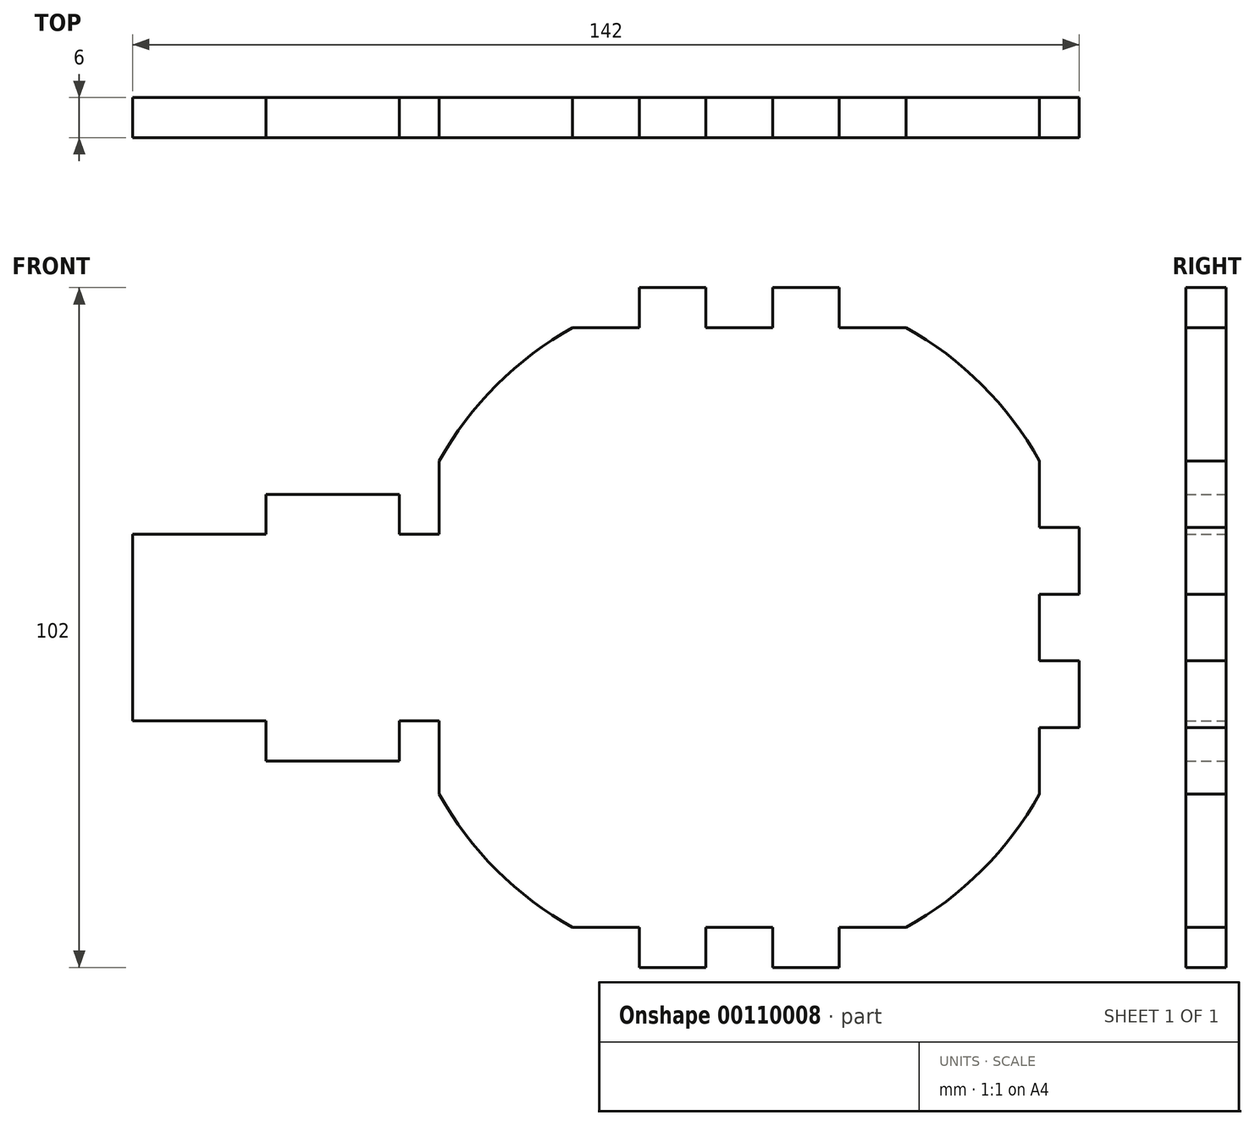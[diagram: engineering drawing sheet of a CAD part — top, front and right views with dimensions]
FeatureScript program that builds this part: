
annotation { "Feature Type Name" : "Feature", "Feature Type Description" : "" }
export const myFeature = defineFeature(function(context is Context, id is Id, definition is map)
    precondition{}
    {
        {
            var Q0;
            Q0=qCreatedBy(makeId("Front.planeOp"),FACE);
            var sketch = newSketch(context, id + "F0", { "sketchPlane" : qUnion([Q0])});
            skLineSegment(sketch, "E0.bottom", {"start": v(53.37, -58.05) * mm, "end": v(43.37, -58.05) * mm});
            skLineSegment(sketch, "E0.top", {"start": v(53.37, 31.95) * mm, "end": v(43.37, 31.95) * mm});
            skLineSegment(sketch, "E0.left", {"start": v(73.37, -38.05) * mm, "end": v(73.37, -28.05) * mm});
            skPoint(sketch, "E0.middle", {"position": v(28.37, -13.05) * mm});
            skArc(sketch, "E1", {"start": v(-16.63, -38.05) * mm, "mid": v(-8.03, -49.46) * mm, "end": v(3.37, -58.05) * mm});
            skPoint(sketch, "E2", {"position": v(-16.63, 11.95) * mm});
            skPoint(sketch, "E3", {"position": v(-16.63, -38.05) * mm});
            skArc(sketch, "E4.trimOffspring", {"start": v(73.37, 11.95) * mm, "mid": v(64.77, 23.35) * mm, "end": v(53.37, 31.95) * mm});
            skArc(sketch, "E5.trimOffspring", {"start": v(3.37, 31.95) * mm, "mid": v(-8.03, 23.35) * mm, "end": v(-16.63, 11.95) * mm});
            skArc(sketch, "E6.trimOffspring", {"start": v(53.37, -58.05) * mm, "mid": v(64.77, -49.46) * mm, "end": v(73.37, -38.05) * mm});
            skPoint(sketch, "E7.orphan", {"position": v(-16.63, -58.05) * mm});
            skPoint(sketch, "E8.orphan", {"position": v(73.37, -58.05) * mm});
            skPoint(sketch, "E9.orphan", {"position": v(73.37, 31.95) * mm});
            skPoint(sketch, "E10.orphan", {"position": v(-16.63, 31.95) * mm});
            skLineSegment(sketch, "E11.top", {"start": v(13.37, 37.95) * mm, "end": v(23.37, 37.95) * mm});
            skLineSegment(sketch, "E11.left", {"start": v(13.37, 37.95) * mm, "end": v(13.37, 31.95) * mm});
            skLineSegment(sketch, "E11.right", {"start": v(23.37, 37.95) * mm, "end": v(23.37, 31.95) * mm});
            skLineSegment(sketch, "E12.trimOffspring", {"start": v(13.37, 31.95) * mm, "end": v(3.37, 31.95) * mm});
            skLineSegment(sketch, "E13.MirrorCS", {"start": v(43.37, 37.95) * mm, "end": v(33.37, 37.95) * mm});
            skLineSegment(sketch, "E14.MirrorCS", {"start": v(43.37, 37.95) * mm, "end": v(43.37, 31.95) * mm});
            skLineSegment(sketch, "E15.MirrorCS", {"start": v(33.37, 37.95) * mm, "end": v(33.37, 31.95) * mm});
            skLineSegment(sketch, "E16.MirrorCS", {"start": v(79.37, 1.95) * mm, "end": v(73.37, 1.95) * mm});
            skLineSegment(sketch, "E17.MirrorCS", {"start": v(79.37, -8.05) * mm, "end": v(73.37, -8.05) * mm});
            skLineSegment(sketch, "E18.MirrorCS", {"start": v(79.37, 1.95) * mm, "end": v(79.37, -8.05) * mm});
            skLineSegment(sketch, "E19.trimOffspring", {"start": v(33.37, 31.95) * mm, "end": v(23.37, 31.95) * mm});
            skLineSegment(sketch, "E20.trimOffspring", {"start": v(73.37, 1.95) * mm, "end": v(73.37, 11.95) * mm});
            skLineSegment(sketch, "E21.MirrorCS", {"start": v(79.37, -18.05) * mm, "end": v(73.37, -18.05) * mm});
            skLineSegment(sketch, "E22.MirrorCS", {"start": v(79.37, -28.05) * mm, "end": v(73.37, -28.05) * mm});
            skLineSegment(sketch, "E23.MirrorCS", {"start": v(79.37, -28.05) * mm, "end": v(79.37, -18.05) * mm});
            skLineSegment(sketch, "E24.MirrorCS", {"start": v(33.37, -64.05) * mm, "end": v(33.37, -58.05) * mm});
            skLineSegment(sketch, "E25.MirrorCS", {"start": v(43.37, -64.05) * mm, "end": v(43.37, -58.05) * mm});
            skLineSegment(sketch, "E26.MirrorCS", {"start": v(13.37, -64.05) * mm, "end": v(13.37, -58.05) * mm});
            skLineSegment(sketch, "E27.MirrorCS", {"start": v(23.37, -64.05) * mm, "end": v(23.37, -58.05) * mm});
            skLineSegment(sketch, "E28.MirrorCS", {"start": v(43.37, -64.05) * mm, "end": v(33.37, -64.05) * mm});
            skLineSegment(sketch, "E29.MirrorCS", {"start": v(13.37, -64.05) * mm, "end": v(23.37, -64.05) * mm});
            skLineSegment(sketch, "E30.trimOffspring", {"start": v(73.37, -18.05) * mm, "end": v(73.37, -8.05) * mm});
            skLineSegment(sketch, "E31.trimOffspring", {"start": v(13.37, -58.05) * mm, "end": v(3.37, -58.05) * mm});
            skLineSegment(sketch, "E32.trimOffspring", {"start": v(33.37, -58.05) * mm, "end": v(23.37, -58.05) * mm});
            skLineSegment(sketch, "E33", {"start": v(-16.63, 11.95) * mm, "end": v(-16.63, 0.95) * mm});
            skLineSegment(sketch, "E34", {"start": v(-16.63, 0.95) * mm, "end": v(-22.63, 0.95) * mm});
            skLineSegment(sketch, "E35", {"start": v(-62.63, 0.95) * mm, "end": v(-62.63, -27.05) * mm});
            skLineSegment(sketch, "E36", {"start": v(-62.63, -27.05) * mm, "end": v(-42.63, -27.05) * mm});
            skLineSegment(sketch, "E37", {"start": v(-16.63, -27.05) * mm, "end": v(-16.63, -38.05) * mm});
            skLineSegment(sketch, "E38.top", {"start": v(-22.63, 6.95) * mm, "end": v(-42.63, 6.95) * mm});
            skLineSegment(sketch, "E38.left", {"start": v(-22.63, 0.95) * mm, "end": v(-22.63, 6.95) * mm});
            skLineSegment(sketch, "E38.right", {"start": v(-42.63, 0.95) * mm, "end": v(-42.63, 6.95) * mm});
            skLineSegment(sketch, "E39.trimOffspring", {"start": v(-42.63, 0.95) * mm, "end": v(-62.63, 0.95) * mm});
            skLineSegment(sketch, "E40.top", {"start": v(-22.63, -33.05) * mm, "end": v(-42.63, -33.05) * mm});
            skLineSegment(sketch, "E40.left", {"start": v(-22.63, -27.05) * mm, "end": v(-22.63, -33.05) * mm});
            skLineSegment(sketch, "E40.right", {"start": v(-42.63, -27.05) * mm, "end": v(-42.63, -33.05) * mm});
            skLineSegment(sketch, "E41.trimOffspring", {"start": v(-22.63, -27.05) * mm, "end": v(-16.63, -27.05) * mm});
            skSolve(sketch);
        }
        {
            var Q0;
            Q0 = qSketchRegion(id + "F0", true);
            extrude(context, id + "F1", {"entities" : qUnion([Q0]), "depth" : 6 * mm});
        }
    });
